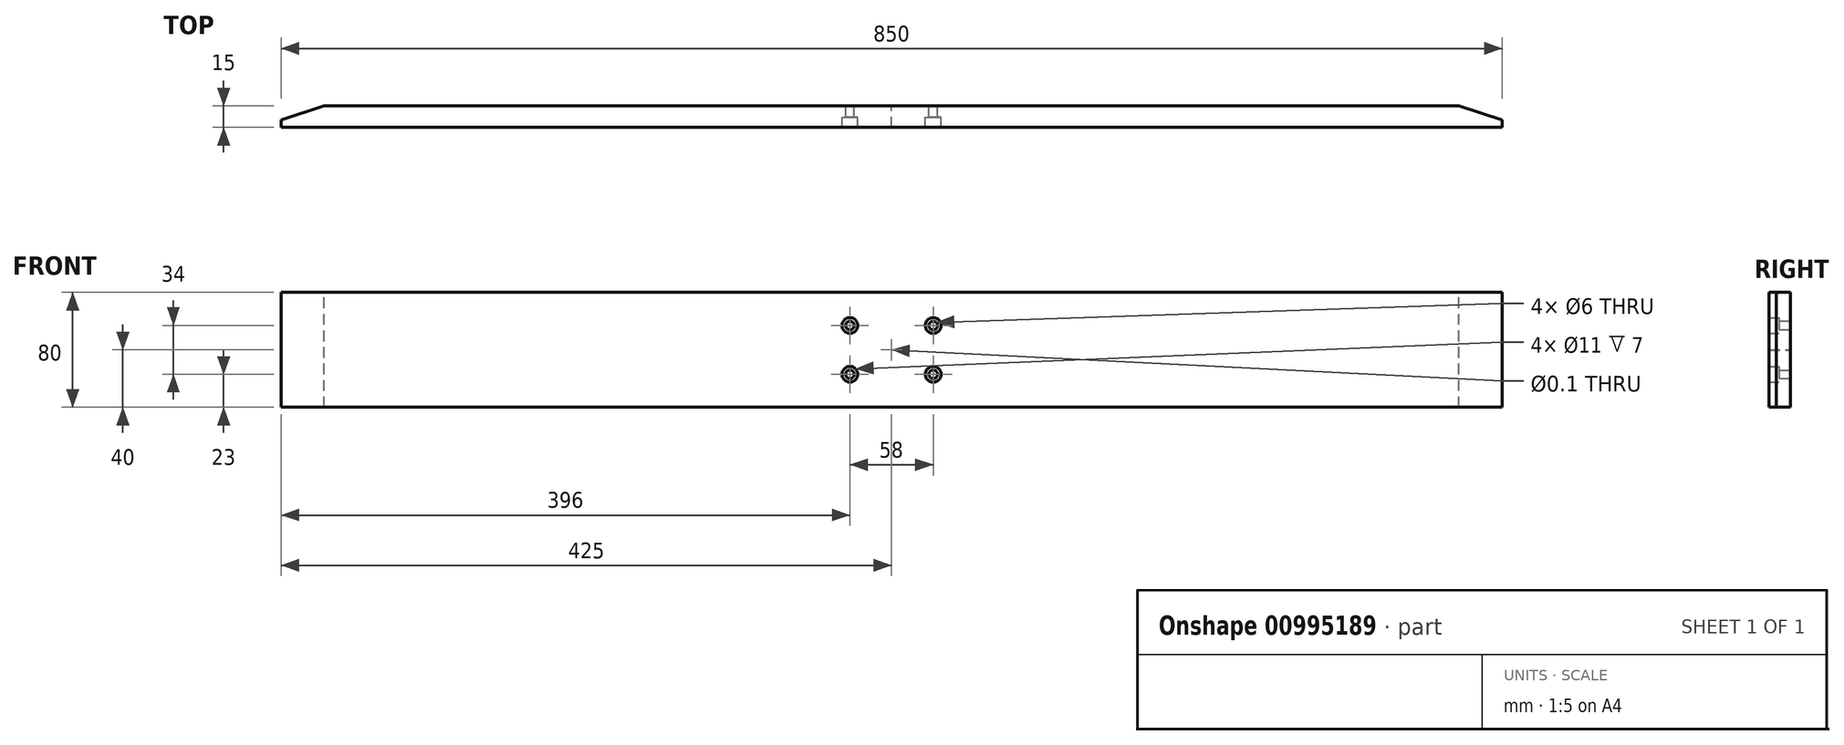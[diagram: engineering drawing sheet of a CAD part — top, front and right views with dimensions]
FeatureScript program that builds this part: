
annotation { "Feature Type Name" : "Feature", "Feature Type Description" : "" }
export const myFeature = defineFeature(function(context is Context, id is Id, definition is map)
    precondition{}
    {
        {
            var Q0;
            Q0=qCreatedBy(makeId("Front.planeOp"),FACE);
            var sketch = newSketch(context, id + "F0", { "sketchPlane" : qUnion([Q0])});
            skLineSegment(sketch, "E0.bottom", {"start": v(-425, 40) * mm, "end": v(425, 40) * mm});
            skLineSegment(sketch, "E0.top", {"start": v(-425, -40) * mm, "end": v(425, -40) * mm});
            skLineSegment(sketch, "E0.left", {"start": v(-425, 40) * mm, "end": v(-425, -40) * mm});
            skLineSegment(sketch, "E0.right", {"start": v(425, 40) * mm, "end": v(425, -40) * mm});
            skPoint(sketch, "E0.middle", {"position": v(0, 0) * mm});
            skSolve(sketch);
        }
        {
            var Q0;
            Q0=makeQuery(id+"F0.imprint","IMPRINT",FACE,{"disambiguationData":[TD([[makeQuery(id+"F0.imprint","IMPRINT",EDGE,{"derivedFrom":sQuery(id+"F0.wireOp",EDGE,"E0.bottom")}),-1.0]])]});
            extrude(context, id + "F1", {"entities" : qUnion([Q0]), "depth" : 15 * mm, "offsetDistance" : 25 * mm, "symmetric" : true});
        }
        {
            var Q0;
            Q0=makeQuery(id+"F1.opExtrude","CAP_FACE",FACE,{"disambiguationData":[OSD([sQuery(id+"F0.wireOp",EDGE,"E0.bottom"),sQuery(id+"F0.wireOp",EDGE,"E0.top"),sQuery(id+"F0.wireOp",EDGE,"E0.left"),sQuery(id+"F0.wireOp",EDGE,"E0.right")])],"isStart":false});
            var sketch = newSketch(context, id + "F2", { "sketchPlane" : qUnion([Q0])});
            skLineSegment(sketch, "E1.bottom", {"start": v(-29, 17) * mm, "end": v(29, 17) * mm});
            skLineSegment(sketch, "E1.top", {"start": v(-29, -17) * mm, "end": v(29, -17) * mm});
            skLineSegment(sketch, "E1.left", {"start": v(-29, 17) * mm, "end": v(-29, -17) * mm});
            skLineSegment(sketch, "E1.right", {"start": v(29, 17) * mm, "end": v(29, -17) * mm});
            skPoint(sketch, "E1.middle", {"position": v(0, 0) * mm});
            skSolve(sketch);
        }
        {
            var Q0;
            Q0=sQuery(id+"F2.wireOp",VERTEX,"E1.bottom.start");
            var Q1;
            Q1=sQuery(id+"F2.wireOp",VERTEX,"E1.bottom.end");
            var Q2;
            Q2=sQuery(id+"F2.wireOp",VERTEX,"E1.top.end");
            var Q3;
            Q3=sQuery(id+"F2.wireOp",VERTEX,"E1.top.start");
            var Q4;
            Q4=makeQuery(id+"F1.opExtrude","SWEPT_BODY",BODY,{"disambiguationData":[OSD([sQuery(id+"F0.wireOp",EDGE,"E0.bottom"),sQuery(id+"F0.wireOp",EDGE,"E0.top"),sQuery(id+"F0.wireOp",EDGE,"E0.left"),sQuery(id+"F0.wireOp",EDGE,"E0.right")])]});
            hole(context, id + "F3", {"style" : HoleStyle.C_BORE, "endStyle" : HoleEndStyle.THROUGH, "holeDiameter" : 6 * mm, "cBoreDiameter" : 11 * mm, "cBoreDepth" : 7 * mm, "majorDiameter" : 5 * mm, "isTappedThrough" : true, "tappedDepth" : 12 * mm, "tapClearance" : 3, "locations" : qUnion([Q0, Q1, Q2, Q3]), "scope" : qUnion([Q4]), "startStyle" : HoleStartStyle.PART});
        }
        {
            var Q0;
            Q0=sQuery(id+"F2.wireOp",VERTEX,"E1.middle");
            var Q1;
            Q1=makeQuery(id+"F1.opExtrude","SWEPT_BODY",BODY,{"disambiguationData":[OSD([sQuery(id+"F0.wireOp",EDGE,"E0.bottom"),sQuery(id+"F0.wireOp",EDGE,"E0.top"),sQuery(id+"F0.wireOp",EDGE,"E0.left"),sQuery(id+"F0.wireOp",EDGE,"E0.right")])]});
            hole(context, id + "F4", {"style" : HoleStyle.SIMPLE, "endStyle" : HoleEndStyle.THROUGH, "holeDiameter" : 0.1 * mm, "majorDiameter" : 5 * mm, "isTappedThrough" : true, "tappedDepth" : 12 * mm, "tapClearance" : 3, "locations" : qUnion([Q0]), "scope" : qUnion([Q1]), "startStyle" : HoleStartStyle.PART});
        }
        {
            var Q0;
            Q0=makeQuery(id+"F1.opExtrude","SWEPT_FACE",FACE,{"disambiguationData":[OSD([sQuery(id+"F0.wireOp",EDGE,"E0.bottom")])]});
            var sketch = newSketch(context, id + "F5", { "sketchPlane" : qUnion([Q0])});
            skLineSegment(sketch, "E2", {"start": v(-425, 7.5) * mm, "end": v(-425, -2.5) * mm});
            skLineSegment(sketch, "E3", {"start": v(-425, -2.5) * mm, "end": v(-395, 7.5) * mm});
            skLineSegment(sketch, "E4", {"start": v(-395, 7.5) * mm, "end": v(-425, 7.5) * mm});
            skLineSegment(sketch, "E5", {"start": v(425, 7.5) * mm, "end": v(425, -2.5) * mm});
            skLineSegment(sketch, "E6", {"start": v(425, -2.5) * mm, "end": v(395, 7.5) * mm});
            skLineSegment(sketch, "E7", {"start": v(395, 7.5) * mm, "end": v(425, 7.5) * mm});
            skSolve(sketch);
        }
        {
            var Q0;
            Q0=makeQuery(id+"F5.imprint","IMPRINT",FACE,{"disambiguationData":[TD([[makeQuery(id+"F5.imprint","IMPRINT",EDGE,{"derivedFrom":sQuery(id+"F5.wireOp",EDGE,"E2")}),-1.0]])]});
            var Q1;
            Q1=makeQuery(id+"F5.imprint","IMPRINT",FACE,{"disambiguationData":[TD([[makeQuery(id+"F5.imprint","IMPRINT",EDGE,{"derivedFrom":sQuery(id+"F5.wireOp",EDGE,"E5")}),1.0]])]});
            extrude(context, id + "F6", {"entities" : qUnion([Q0, Q1]), "operationType" : NewBodyOperationType.REMOVE, "endBound" : BoundingType.THROUGH_ALL, "oppositeDirection" : true, "depth" : 25 * mm, "offsetDistance" : 25 * mm});
        }
    });
